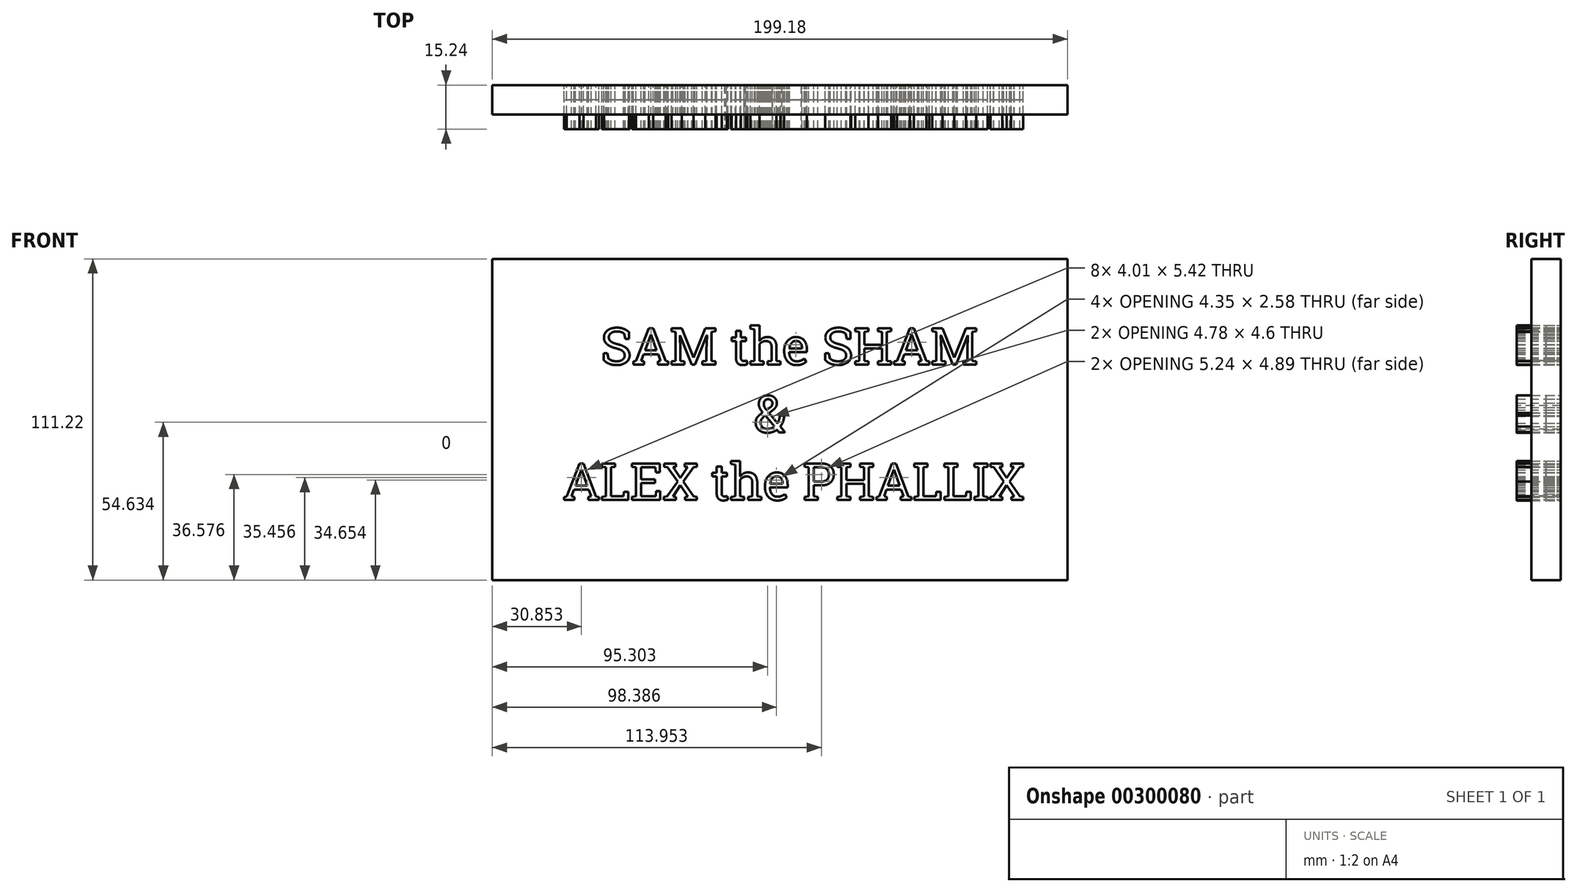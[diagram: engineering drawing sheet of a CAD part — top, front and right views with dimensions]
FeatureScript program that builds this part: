
annotation { "Feature Type Name" : "Feature", "Feature Type Description" : "" }
export const myFeature = defineFeature(function(context is Context, id is Id, definition is map)
    precondition{}
    {
        {
            var Q0;
            Q0=qCreatedBy(makeId("Front.planeOp"),FACE);
            var sketch = newSketch(context, id + "F0", { "sketchPlane" : qUnion([Q0])});
            skLineSegment(sketch, "E0.bottom", {"start": v(-99.59, -55.61) * mm, "end": v(99.59, -55.61) * mm});
            skLineSegment(sketch, "E0.top", {"start": v(-99.59, 55.61) * mm, "end": v(99.59, 55.61) * mm});
            skLineSegment(sketch, "E0.left", {"start": v(-99.59, -55.61) * mm, "end": v(-99.59, 55.61) * mm});
            skLineSegment(sketch, "E0.right", {"start": v(99.59, -55.61) * mm, "end": v(99.59, 55.61) * mm});
            skPoint(sketch, "E0.middle", {"position": v(0, 0) * mm});
            skSolve(sketch);
        }
        {
            var Q0;
            Q0=qCreatedBy(makeId("Front.planeOp"),FACE);
            var sketch = newSketch(context, id + "F1", { "sketchPlane" : qUnion([Q0])});
            skText(sketch, "E1", { "text": "          SAM the SHAM\n                      &\n       ALEX the PHALLIX", "fontName": "RobotoSlab-Regular.ttf"});
            const initialGuessF1  = {"E1": [-0.10618, 0.01902, 1, 0, 0.01279]};
            skSetInitialGuess(sketch, initialGuessF1);
            skSolve(sketch);
        }
        {
            var Q0;
            Q0 = qSketchRegion(id + "F1", true);
            var Q1;
            Q1 = qConstructionFilter(qBodyType(qCreatedBy(id + "F1" ,EDGE), BodyType.WIRE), ConstructionObject.NO);
            extrude(context, id + "F2", {"entities" : qUnion([Q0]), "surfaceEntities" : qUnion([Q1]), "depth" : 5.08 * mm});
        }
        {
            var Q0;
            Q0=sQuery(id+"F0.wireOp",EDGE,"E0.right");
            extrude(context, id + "F3", {"bodyType" : ToolBodyType.SURFACE, "surfaceEntities" : qUnion([Q0]), "depth" : 10.16 * mm});
        }
        {
            var Q0;
            Q0 = qSketchRegion(id + "F0", true);
            extrude(context, id + "F4", {"entities" : qUnion([Q0]), "depth" : 10.16 * mm});
        }
        {
            var Q0;
            Q0 = qSketchRegion(id + "F1", true);
            extrude(context, id + "F5", {"entities" : qUnion([Q0]), "depth" : 15.24 * mm});
        }
    });
